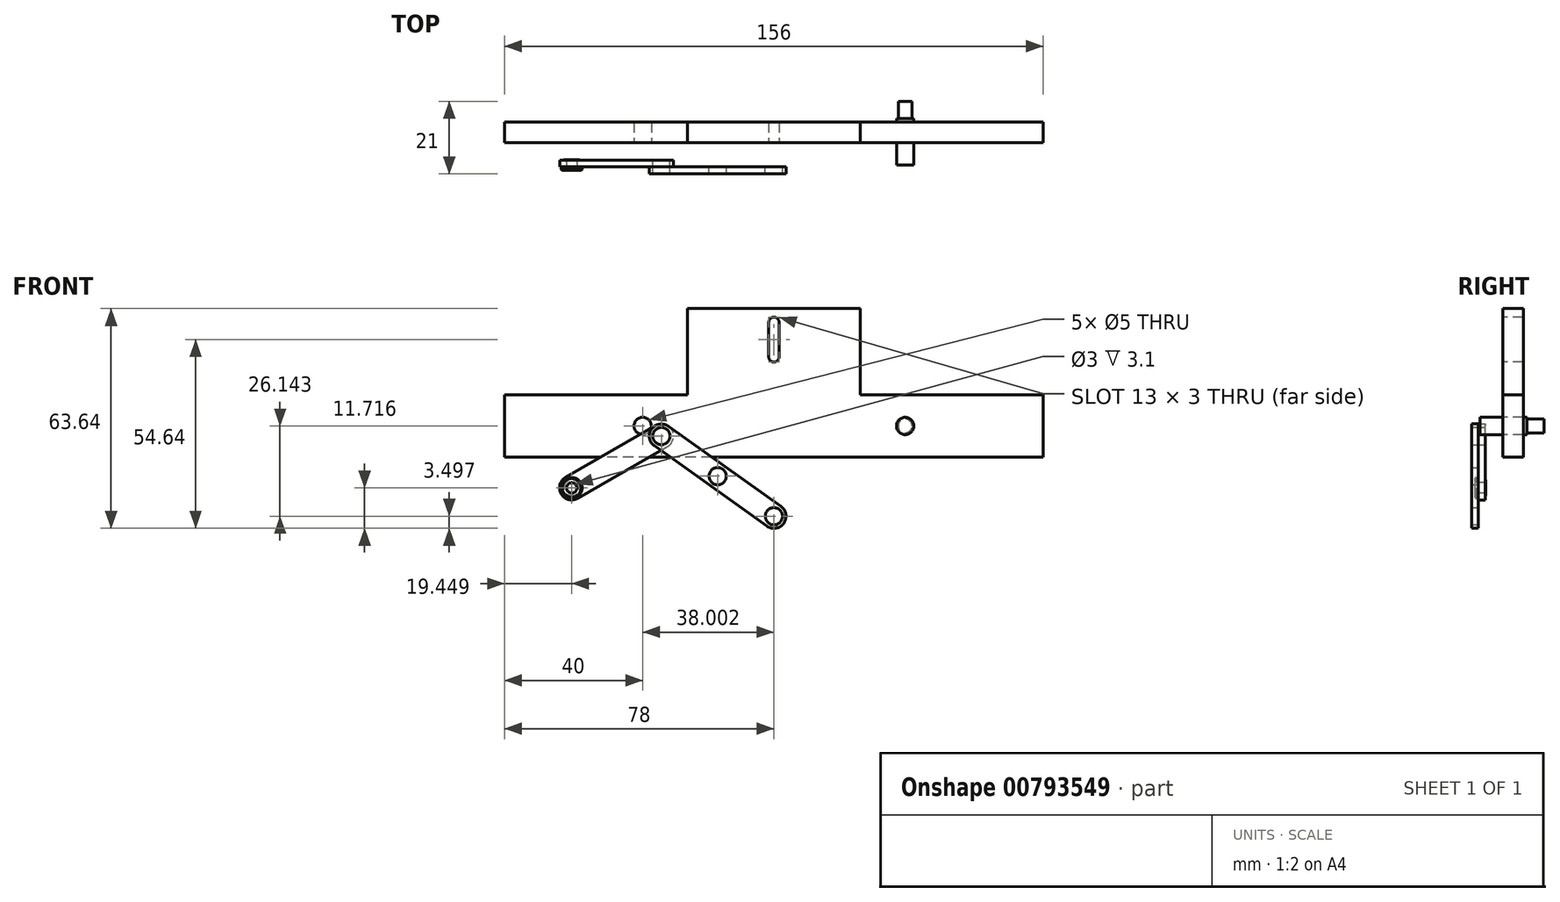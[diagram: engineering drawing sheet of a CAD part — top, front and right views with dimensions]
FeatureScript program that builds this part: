
annotation { "Feature Type Name" : "Feature", "Feature Type Description" : "" }
export const myFeature = defineFeature(function(context is Context, id is Id, definition is map)
    precondition{}
    {
        {
            var Q0;
            Q0=qCreatedBy(makeId("Top.planeOp"),FACE);
            var sketch = newSketch(context, id + "F0", { "sketchPlane" : qUnion([Q0])});
            skLineSegment(sketch, "E0", {"start": v(-78, -35.5) * mm, "end": v(78, -35.5) * mm});
            skLineSegment(sketch, "E1", {"start": v(78, -35.5) * mm, "end": v(78, -41.5) * mm});
            skLineSegment(sketch, "E2", {"start": v(78, -41.5) * mm, "end": v(-78, -41.5) * mm});
            skLineSegment(sketch, "E3", {"start": v(-78, -41.5) * mm, "end": v(-78, -35.5) * mm});
            skLineSegment(sketch, "E4", {"start": v(0, -35.5) * mm, "end": v(0, -41.5) * mm, "construction": true});
            skLineSegment(sketch, "E5", {"start": v(-38, -35.5) * mm, "end": v(-38, -41.5) * mm, "construction": true});
            skLineSegment(sketch, "E6", {"start": v(38, -35.5) * mm, "end": v(38, -41.5) * mm, "construction": true});
            skSolve(sketch);
        }
        {
            var Q0;
            Q0 = qSketchRegion(id + "F0", true);
            extrude(context, id + "F1", {"entities" : qUnion([Q0]), "endBound" : BoundingType.SYMMETRIC, "depth" : 18 * mm, "offsetDistance" : 25 * mm});
        }
        {
            var Q0;
            Q0=makeQuery(id+"F1.opExtrude","SWEPT_FACE",FACE,{"disambiguationData":[OSD([sQuery(id+"F0.wireOp",EDGE,"E2")])]});
            var sketch = newSketch(context, id + "F2", { "sketchPlane" : qUnion([Q0])});
            skCircle(sketch, "E7", {"center": v(-38, 0) * mm, "radius": 2.5 * mm});
            skCircle(sketch, "E8", {"center": v(38, 0) * mm, "radius": 2.5 * mm});
            skSolve(sketch);
        }
        {
            var Q0;
            Q0 = qSketchRegion(id + "F2", true);
            extrude(context, id + "F3", {"entities" : qUnion([Q0]), "operationType" : NewBodyOperationType.REMOVE, "endBound" : BoundingType.UP_TO_NEXT, "oppositeDirection" : true, "depth" : 25 * mm, "offsetDistance" : 25 * mm});
        }
        {
            var Q0;
            Q0=makeQuery(id+"F1.opExtrude","SWEPT_FACE",FACE,{"disambiguationData":[OSD([sQuery(id+"F0.wireOp",EDGE,"E2")])]});
            cPlane(context, id + "F4", {"entities" : qUnion([Q0]), "cplaneType" : CPlaneType.OFFSET, "offset" : 5 * mm, "width" : 150 * mm, "height" : 150 * mm});
        }
        {
            var Q0;
            Q0=makeQuery(id+"F1.opExtrude","SWEPT_FACE",FACE,{"disambiguationData":[OSD([sQuery(id+"F0.wireOp",EDGE,"E2")])]});
            var sketch = newSketch(context, id + "F5", { "sketchPlane" : qUnion([Q0])});
            skCircle(sketch, "E9.0", {"center": v(38, 0) * mm, "radius": 2.5 * mm});
            skSolve(sketch);
        }
        {
            var Q0;
            Q0 = qSketchRegion(id + "F5", true);
            extrude(context, id + "F6", {"entities" : qUnion([Q0]), "oppositeDirection" : true, "depth" : 7 * mm, "offsetDistance" : 25 * mm});
        }
        {
            var Q0;
            Q0=makeQuery(id+"F6.opExtrude","CAP_FACE",FACE,{"disambiguationData":[OSD([sQuery(id+"F5.wireOp",EDGE,"E9.0")])],"isStart":false});
            var sketch = newSketch(context, id + "F7", { "sketchPlane" : qUnion([Q0])});
            skCircle(sketch, "E10", {"center": v(-38, 0) * mm, "radius": 2 * mm});
            skSolve(sketch);
        }
        {
            var Q0;
            Q0 = qSketchRegion(id + "F7", true);
            extrude(context, id + "F8", {"entities" : qUnion([Q0]), "operationType" : NewBodyOperationType.ADD, "depth" : 5 * mm, "offsetDistance" : 25 * mm});
        }
        {
            var Q0;
            Q0=makeQuery(id+"F6.opExtrude","CAP_FACE",FACE,{"disambiguationData":[OSD([sQuery(id+"F5.wireOp",EDGE,"E9.0")])],"isStart":true});
            var sketch = newSketch(context, id + "F9", { "sketchPlane" : qUnion([Q0])});
            skCircle(sketch, "E11.0", {"center": v(38, 0) * mm, "radius": 2.5 * mm});
            skSolve(sketch);
        }
        {
            var Q0;
            Q0 = qSketchRegion(id + "F9", true);
            extrude(context, id + "F10", {"entities" : qUnion([Q0]), "operationType" : NewBodyOperationType.ADD, "depth" : 6.5 * mm, "offsetDistance" : 25 * mm});
        }
        {
            var Q0;
            Q0=makeQuery(id+"F1.opExtrude","CAP_FACE",FACE,{"disambiguationData":[OSD([sQuery(id+"F0.wireOp",EDGE,"E0"),sQuery(id+"F0.wireOp",EDGE,"E1"),sQuery(id+"F0.wireOp",EDGE,"E2"),sQuery(id+"F0.wireOp",EDGE,"E3")])],"isStart":false});
            var sketch = newSketch(context, id + "F11", { "sketchPlane" : qUnion([Q0])});
            skLineSegment(sketch, "E12.bottom", {"start": v(-25, -41.5) * mm, "end": v(25, -41.5) * mm});
            skLineSegment(sketch, "E12.top", {"start": v(-25, -35.5) * mm, "end": v(25, -35.5) * mm});
            skLineSegment(sketch, "E12.left", {"start": v(-25, -41.5) * mm, "end": v(-25, -35.5) * mm});
            skLineSegment(sketch, "E12.right", {"start": v(25, -41.5) * mm, "end": v(25, -35.5) * mm});
            skLineSegment(sketch, "E13", {"start": v(0, -35.5) * mm, "end": v(0, -41.5) * mm, "construction": true});
            skSolve(sketch);
        }
        {
            var Q0;
            Q0 = qSketchRegion(id + "F11", true);
            extrude(context, id + "F12", {"entities" : qUnion([Q0]), "operationType" : NewBodyOperationType.ADD, "depth" : 25 * mm, "offsetDistance" : 25 * mm});
        }
        {
            var Q0;
            Q0=makeQuery(id+"F12.boolean.opBoolean","MERGE",FACE,{"derivedFrom":[makeQuery(id+"F1.opExtrude","SWEPT_FACE",FACE,{"disambiguationData":[OSD([sQuery(id+"F0.wireOp",EDGE,"E2")])]}),makeQuery(id+"F12.opExtrude","SWEPT_FACE",FACE,{"disambiguationData":[OSD([sQuery(id+"F11.wireOp",EDGE,"E12.bottom")])]})]});
            var sketch = newSketch(context, id + "F13", { "sketchPlane" : qUnion([Q0])});
            skLineSegment(sketch, "E14", {"start": v(0, 30) * mm, "end": v(0, 20) * mm, "construction": true});
            skArc(sketch, "E15.0.startCap", {"start": v(-1.5, 30) * mm, "mid": v(0, 31.5) * mm, "end": v(1.5, 30) * mm});
            skArc(sketch, "E15.0.endCap", {"start": v(1.5, 20) * mm, "mid": v(0, 18.5) * mm, "end": v(-1.5, 20) * mm});
            skLineSegment(sketch, "E15.0.left", {"start": v(1.5, 30) * mm, "end": v(1.5, 20) * mm});
            skLineSegment(sketch, "E15.0.right", {"start": v(-1.5, 30) * mm, "end": v(-1.5, 20) * mm});
            skSolve(sketch);
        }
        {
            var Q0;
            Q0 = qSketchRegion(id + "F13", true);
            extrude(context, id + "F14", {"entities" : qUnion([Q0]), "operationType" : NewBodyOperationType.REMOVE, "endBound" : BoundingType.UP_TO_NEXT, "oppositeDirection" : true, "depth" : 25 * mm, "offsetDistance" : 25 * mm});
        }
        {
            var Q0;
            Q0=qCreatedBy(id+"F4.planeOp",FACE);
            var sketch = newSketch(context, id + "F15", { "sketchPlane" : qUnion([Q0])});
            skLineSegment(sketch, "E16", {"start": v(-58.55, -17.92) * mm, "end": v(-32.57, -2.92) * mm, "construction": true});
            skCircle(sketch, "E17", {"center": v(-58.55, -17.92) * mm, "radius": 2.5 * mm});
            skCircle(sketch, "E18", {"center": v(-32.57, -2.92) * mm, "radius": 2.5 * mm});
            skArc(sketch, "E19.0.startCap", {"start": v(-56.8, -20.96) * mm, "mid": v(-61.58, -19.67) * mm, "end": v(-60.3, -14.9) * mm});
            skArc(sketch, "E19.0.endCap", {"start": v(-34.32, 0.1) * mm, "mid": v(-29.54, -1.17) * mm, "end": v(-30.82, -5.96) * mm});
            skLineSegment(sketch, "E19.0.left", {"start": v(-60.3, -14.9) * mm, "end": v(-34.32, 0.1) * mm});
            skLineSegment(sketch, "E19.0.right", {"start": v(-56.8, -20.96) * mm, "end": v(-30.82, -5.96) * mm});
            skSolve(sketch);
        }
        {
            var Q0;
            Q0 = qSketchRegion(id + "F15", true);
            extrude(context, id + "F16", {"entities" : qUnion([Q0]), "depth" : 2 * mm, "offsetDistance" : 25 * mm});
        }
        {
            var Q0;
            Q0=makeQuery(id+"F16.opExtrude","CAP_FACE",FACE,{"disambiguationData":[OSD([sQuery(id+"F15.wireOp",EDGE,"E17"),sQuery(id+"F15.wireOp",EDGE,"E18"),sQuery(id+"F15.wireOp",EDGE,"E19.0.startCap"),sQuery(id+"F15.wireOp",EDGE,"E19.0.endCap"),sQuery(id+"F15.wireOp",EDGE,"E19.0.left"),sQuery(id+"F15.wireOp",EDGE,"E19.0.right")])],"isStart":false});
            var sketch = newSketch(context, id + "F17", { "sketchPlane" : qUnion([Q0])});
            skLineSegment(sketch, "E20", {"start": v(-32.57, -2.92) * mm, "end": v(0, -26.14) * mm, "construction": true});
            skCircle(sketch, "E21", {"center": v(-32.57, -2.92) * mm, "radius": 2.5 * mm});
            skCircle(sketch, "E22", {"center": v(0, -26.14) * mm, "radius": 2.5 * mm});
            skArc(sketch, "E23.0.startCap", {"start": v(-34.6, -5.77) * mm, "mid": v(-35.42, -0.9) * mm, "end": v(-30.54, -0.07) * mm});
            skArc(sketch, "E23.0.endCap", {"start": v(2.03, -23.3) * mm, "mid": v(2.85, -28.17) * mm, "end": v(-2.03, -29) * mm});
            skLineSegment(sketch, "E23.0.left", {"start": v(-30.54, -0.07) * mm, "end": v(2.03, -23.3) * mm});
            skLineSegment(sketch, "E23.0.right", {"start": v(-34.6, -5.77) * mm, "end": v(-2.03, -29) * mm});
            skCircle(sketch, "E24", {"center": v(-16.28, -14.53) * mm, "radius": 2.5 * mm});
            skSolve(sketch);
        }
        {
            var Q0;
            Q0 = qSketchRegion(id + "F17", true);
            extrude(context, id + "F18", {"entities" : qUnion([Q0]), "depth" : 2 * mm, "offsetDistance" : 25 * mm});
        }
        {
            var Q0;
            Q0=makeQuery(id+"F16.opExtrude","CAP_FACE",FACE,{"disambiguationData":[OSD([sQuery(id+"F15.wireOp",EDGE,"E17"),sQuery(id+"F15.wireOp",EDGE,"E18"),sQuery(id+"F15.wireOp",EDGE,"E19.0.startCap"),sQuery(id+"F15.wireOp",EDGE,"E19.0.endCap"),sQuery(id+"F15.wireOp",EDGE,"E19.0.left"),sQuery(id+"F15.wireOp",EDGE,"E19.0.right")])],"isStart":false});
            var sketch = newSketch(context, id + "F19", { "sketchPlane" : qUnion([Q0])});
            skCircle(sketch, "E25.0", {"center": v(-58.55, -17.92) * mm, "radius": 2.5 * mm});
            skSolve(sketch);
        }
        {
            var Q0;
            Q0=makeQuery(id+"F19.imprint","IMPRINT",FACE,{"disambiguationData":[TD([[makeQuery(id+"F19.imprint","IMPRINT",EDGE,{"derivedFrom":sQuery(id+"F19.wireOp",EDGE,"E25.0")}),-1.0]])]});
            var sketch = newSketch(context, id + "F20", { "sketchPlane" : qUnion([Q0])});
            skCircle(sketch, "E26.0", {"center": v(-58.55, -17.92) * mm, "radius": 2.5 * mm});
            skSolve(sketch);
        }
        {
            var Q0;
            Q0 = qSketchRegion(id + "F20", true);
            extrude(context, id + "F21", {"entities" : qUnion([Q0]), "oppositeDirection" : true, "depth" : 2.1 * mm, "offsetDistance" : 25 * mm});
        }
        {
            var Q0;
            Q0=makeQuery(id+"F19.imprint","IMPRINT",FACE,{"disambiguationData":[TD([[makeQuery(id+"F19.imprint","IMPRINT",EDGE,{"derivedFrom":sQuery(id+"F19.wireOp",EDGE,"E25.0")}),1.0]])]});
            var sketch = newSketch(context, id + "F22", { "sketchPlane" : qUnion([Q0])});
            skCircle(sketch, "E27", {"center": v(-58.55, -17.92) * mm, "radius": 3 * mm});
            skSolve(sketch);
        }
        {
            var Q0;
            Q0 = qSketchRegion(id + "F22", true);
            extrude(context, id + "F23", {"entities" : qUnion([Q0]), "operationType" : NewBodyOperationType.ADD, "depth" : 1 * mm, "offsetDistance" : 25 * mm});
        }
        {
            var Q0;
            Q0=makeQuery(id+"F23.opExtrude","CAP_FACE",FACE,{"disambiguationData":[OSD([sQuery(id+"F22.wireOp",EDGE,"E27")])],"isStart":false});
            var sketch = newSketch(context, id + "F24", { "sketchPlane" : qUnion([Q0])});
            skCircle(sketch, "E28", {"center": v(-58.55, -17.92) * mm, "radius": 1.5 * mm});
            skSolve(sketch);
        }
        {
            var Q0;
            Q0 = qSketchRegion(id + "F24", true);
            extrude(context, id + "F25", {"entities" : qUnion([Q0]), "operationType" : NewBodyOperationType.REMOVE, "endBound" : BoundingType.UP_TO_NEXT, "oppositeDirection" : true, "depth" : 25 * mm, "offsetDistance" : 25 * mm});
        }
        {
            var Q0;
            Q0=makeQuery(id+"F23.opExtrude","CAP_EDGE",EDGE,{"disambiguationData":[OSD([sQuery(id+"F22.wireOp",EDGE,"E27")])],"isStart":false});
            var Q1;
            Q1=makeQuery(id+"F21.opExtrude","CAP_EDGE",EDGE,{"disambiguationData":[OSD([sQuery(id+"F20.wireOp",EDGE,"E26.0")])],"isStart":false});
            chamfer(context, id + "F26", {"entities" : qUnion([Q0, Q1]), "width" : .25 * mm, "tangentPropagation" : true});
        }
    });
